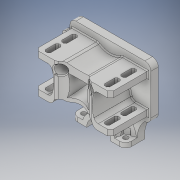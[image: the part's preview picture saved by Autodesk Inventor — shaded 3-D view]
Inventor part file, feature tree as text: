
AUTODESK INVENTOR PART (.ipt)
format: ipt  version: 2018 (Build 220112000, 112)  size: 1,067,008 bytes
history: native  units: in
note: dims shown in document units (in); Inventor stores cm internally (conversion verified against a paired STEP export)
features: extrude x18, sketch x18, fillet x9, projected_geometry x8, chamfer x7, mirror x3
ambient origin geometry x8: Origin, YZ Plane, XZ Plane, XY Plane, X Axis, Y Axis, Z Axis, Center Point
bodies: Solid1 (feature_tree)
feature tree (63):
  extrude  "Extrusion1"  Depth=0.1969in TaperAngle=0.0deg
  extrude  "Extrusion2"  Depth=0.7874in
  fillet  "Fillet1"  Radius=0.126in
  extrude  "Extrusion3"  Depth=0.1575in
  extrude  "Extrusion4"  Depth=0.3937in
  extrude  "Extrusion5"  Depth=0.1969in TaperAngle=0.0deg
  extrude  "Extrusion6"  Depth=0.1496in TaperAngle=0.0deg
  extrude  "Extrusion7"  Depth=0.0394in TaperAngle=0.0deg
  extrude  "Extrusion8"  Depth=0.1575in TaperAngle=0.0deg
  chamfer  "Chamfer1"  Distance=0.1575in
  fillet  "Fillet2"  Radius=0.1575in
  fillet  "Fillet3"  Radius=0.1575in
  extrude  "Extrusion10"  Depth=0.126in
  extrude  "Extrusion13"  Depth=0.1575in
  fillet  "Fillet6"  Radius=0.1575in
  extrude  "Extrusion14"  Depth=0.1575in
  chamfer  "Chamfer2"  Distance=0.9843in
  mirror  "Mirror2"
  chamfer  "Chamfer4"  Distance=0.315in
  chamfer  "Chamfer5"  Distance=0.315in
  extrude  "Extrusion15"  Depth=0.1378in
  chamfer  "Chamfer6"  Distance=0.0984in
  fillet  "Fillet7"  Radius=0.1575in
  extrude  "Extrusion16"  Depth=0.7874in TaperAngle=0.0deg
  mirror  "Mirror3"
  extrude  "Extrusion17"  Depth=0.0984in
  extrude  "Extrusion18"  Depth=0.1181in
  fillet  "Fillet8"  Radius=0.7874in
  extrude  "Extrusion19"  Depth=0.5906in
  fillet  "Fillet9"  Radius=0.2362in
  chamfer  "Chamfer9"  Distance=0.2559in
  chamfer  "Chamfer10"  Distance=0.1575in
  extrude  "Extrusion11"  Depth=0.1575in
  extrude  "Extrusion12"  Depth=0.6693in
  fillet  "Fillet4"  Radius=0.7126in
  mirror  "Mirror1"
  fillet  "Fillet5"  Radius=0.5512in
  sketch  "Sketch1"  dims[d0=2.126in d2=0.1969in d3=0.0in]
  sketch  "Sketch2"  dims[d4=0.7874in d5=0.7874in d6=0.126in]
  sketch  "Sketch3"  dims[d7=0.1969in d8=0.0in d9=0.1575in]
  sketch  "Sketch4"  dims[d10=1.1811in d12=0.3937in]
  sketch  "Sketch5"  dims[d13=0.6339in d14=0.1969in d15=0.0in]
  projected_geometry  "Projected Loop1"
  sketch  "Sketch6"  dims[d16=0.4843in d17=0.1496in d18=0.0709in d19=0.0in d20=0.0in]
  sketch  "Sketch9"  dims[d21=0.1181in d22=0.0394in d23=0.0in]
  projected_geometry  "Projected Loop2"
  projected_geometry  "Projected Loop3"
  sketch  "Sketch10"  dims[d24=0.1181in d25=0.1575in d26=0.0in d29=0.1575in d30=0.0in d31=0.1575in d32=0.0in]
  projected_geometry  "Projected Loop4"
  sketch  "Sketch13"  dims[d33=0.1969in d34=0.0787in d35=45.0deg d43=0.1575in]
  sketch  "Sketch14"  dims[d44=0.1575in d45=0.126in]
  sketch  "Sketch15"  dims[d46=0.1575in d47=0.1575in d48=0.1575in]
  sketch  "Sketch17"  dims[d49=0.1575in d50=0.0in d51=0.1575in]
  sketch  "Sketch18"  dims[d52=0.1575in]
  projected_geometry  "Projected Loop5"
  sketch  "Sketch19"  dims[d53=0.2087in]
  projected_geometry  "Projected Loop6"
  sketch  "Sketch20"  dims[d54=0.5118in]
  projected_geometry  "Projected Loop7"
  sketch  "Sketch21"  dims[d55=1.5354in]
  sketch  "Sketch22"  dims[d56=0.5118in d57=0.9843in d58=0.0in]
  projected_geometry  "Projected Loop8"
  sketch  "Sketch23"  dims[d59=0.1575in d60=0.315in d61=0.315in d62=0.1378in d63=0.0984in d64=0.1575in d65=0.7874in d66=0.0in d67=0.0984in d68=0.1181in d69=0.7874in d70=0.5906in d71=0.2362in d72=0.2559in d73=0.1575in d75=0.1575in d76=0.6693in d77=0.7126in d78=0.5512in d81=0.4331in d82=0.4409in d104=0.7874in d105=0.0787in d106=0.0787in d107=0.9843in d108=0.0in d109=0.1181in d110=0.1378in d111=0.1378in d112=0.0787in d113=0.3543in d114=0.0787in d115=0.3543in d116=1.5748in d117=0.0in d118=0.0394in d119=0.0787in d120=45.0deg d124=0.0787in d125=0.0787in d126=45.0deg d127=0.0276in d128=0.0787in d129=45.0deg d130=0.5906in d131=1.5748in d132=0.0in d133=0.0276in d134=0.0787in d135=45.0deg d136=0.1181in d138=0.2244in d139=0.252in d140=0.3937in d141=0.0in d142=0.2756in d143=0.5118in d144=0.0in d145=0.0in d146=0.0906in d147=0.2559in d148=0.2008in d149=0.3937in d150=0.0in d151=0.0787in d153=0.0787in d154=0.0787in d155=0.0in d164=0.2362in d165=0.0787in d167=0.5118in d168=0.315in d169=0.2362in d170=0.7874in d171=0.0984in d172=45.0deg d173=0.7874in d174=0.0591in d175=45.0deg]
